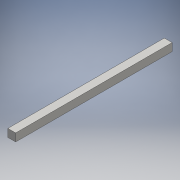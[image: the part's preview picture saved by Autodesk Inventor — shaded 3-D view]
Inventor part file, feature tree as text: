
AUTODESK INVENTOR PART (.ipt)
format: ipt  version: 2016 (Build 200138000, 138)  size: 89,600 bytes
history: native  units: mm
features: other x1, extrude x1, sketch x1
ambient origin geometry x8: Origin, YZ Plane, XZ Plane, XY Plane, X Axis, Y Axis, Z Axis, Center Point
bodies: Body1 (feature_tree)
feature tree (3):
  other  "ソリッド1"
  extrude  "押し出し1"  Depth=20.0mm
  sketch  "スケッチ1"
